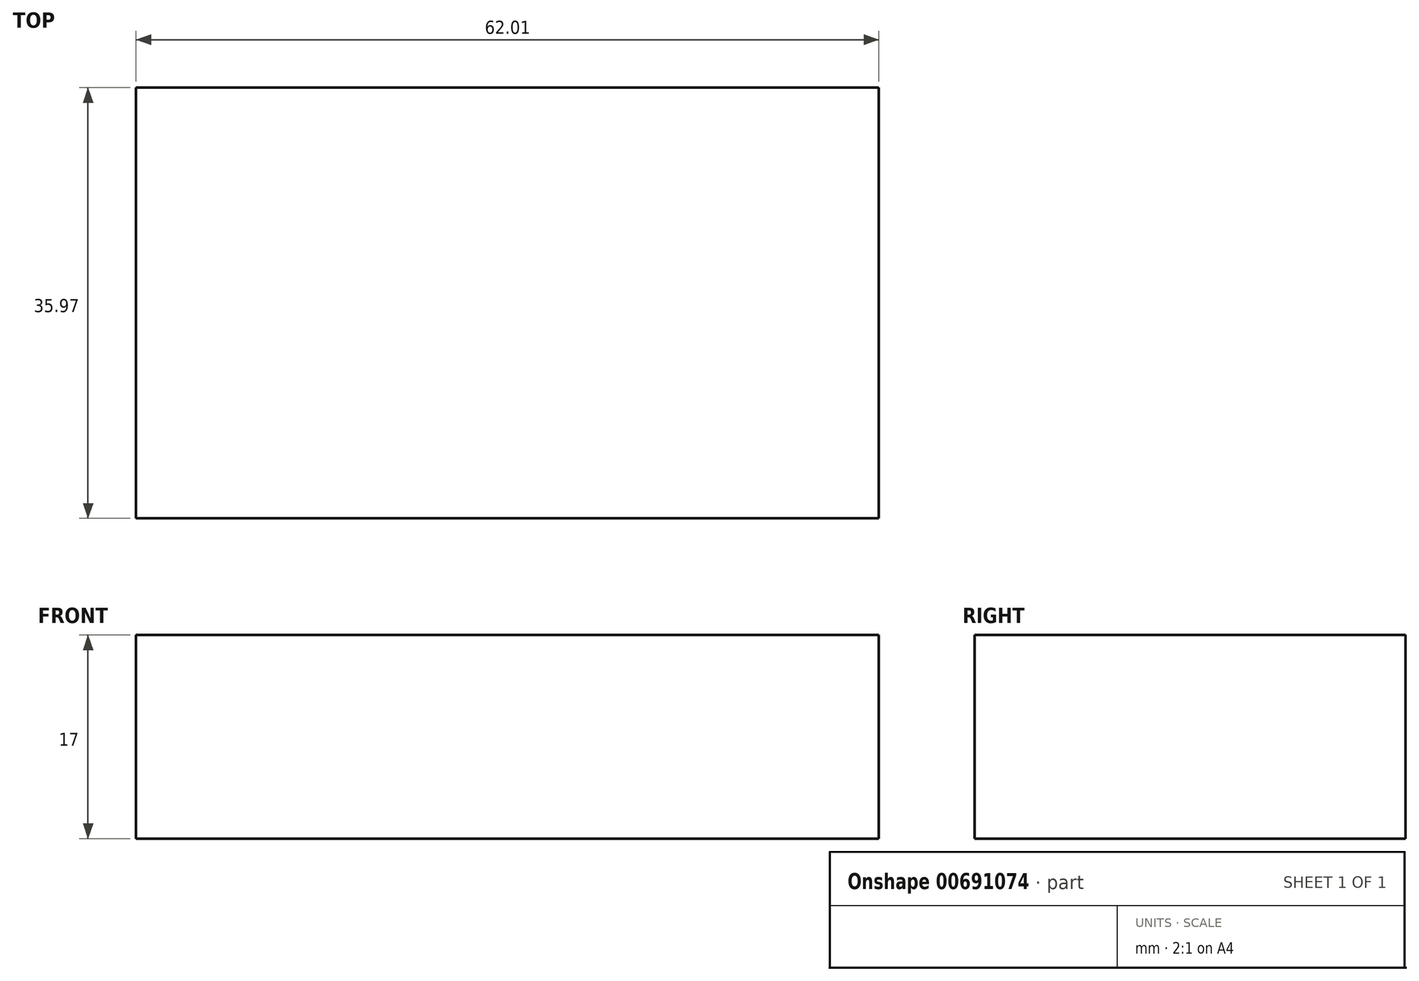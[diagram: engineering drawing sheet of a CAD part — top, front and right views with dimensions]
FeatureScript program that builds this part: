
annotation { "Feature Type Name" : "Feature", "Feature Type Description" : "" }
export const myFeature = defineFeature(function(context is Context, id is Id, definition is map)
    precondition{}
    {
        {
            var Q0;
            Q0=qCreatedBy(makeId("Top.planeOp"),FACE);
            var sketch = newSketch(context, id + "F0", { "sketchPlane" : qUnion([Q0])});
            skLineSegment(sketch, "E0.bottom", {"start": v(-23.45, 8.1) * mm, "end": v(38.56, 8.1) * mm});
            skLineSegment(sketch, "E0.top", {"start": v(-23.45, -27.88) * mm, "end": v(38.56, -27.88) * mm});
            skLineSegment(sketch, "E0.left", {"start": v(-23.45, 8.1) * mm, "end": v(-23.45, -27.88) * mm});
            skLineSegment(sketch, "E0.right", {"start": v(38.56, 8.1) * mm, "end": v(38.56, -27.88) * mm});
            skSolve(sketch);
        }
        {
            var Q0;
            Q0=makeQuery(id+"F0.imprint","IMPRINT",FACE,{"disambiguationData":[TD([[makeQuery(id+"F0.imprint","IMPRINT",EDGE,{"derivedFrom":sQuery(id+"F0.wireOp",EDGE,"E0.bottom")}),-1.0]])]});
            extrude(context, id + "F1", {"entities" : qUnion([Q0]), "depth" : 17 * mm, "offsetDistance" : 25 * mm});
        }
    });
